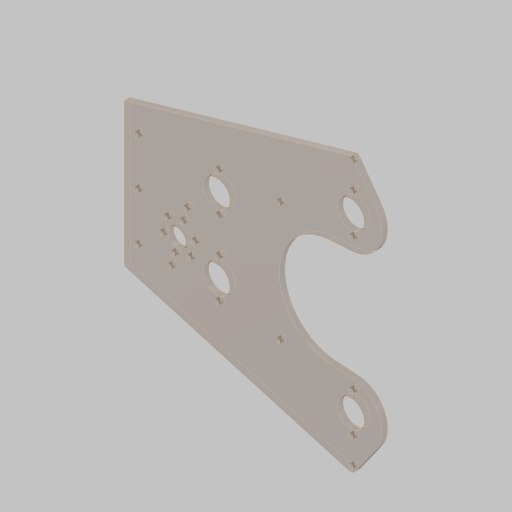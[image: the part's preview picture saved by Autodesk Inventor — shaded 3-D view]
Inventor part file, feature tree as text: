
AUTODESK INVENTOR PART (.ipt)
format: ipt  version: 2023.5 (Build 275446000, 446)  size: 201,728 bytes
history: native  units: in
note: dims shown in document units (in); Inventor stores cm internally (conversion verified against a paired STEP export)
features: sketch x1, extrude x1, hole x1
ambient origin geometry x8: Origin, YZ Plane, XZ Plane, XY Plane, X Axis, Y Axis, Z Axis, Center Point
bodies: Solid1 (feature_tree)
feature tree (3):
  sketch  "Sketch1"  dims[d0=3.0in d1=3.0in d2=4.5in d4=7.2284in d5=1.125in d6=0.75in d7=1.128in d8=1.88in d9=3.125in d10=5.6298in d11=5.992in d12=1.125in d13=0.4688in d14=0.75in d15=1.375in d16=2.3622in d18=360.0deg d20=0.25in d21=1.5in d22=1.0in d23=6.0in d24=9.5in d26=5.0in d27=0.25in d28=0.0in d29=0.375in d30=0.25in d32=1.655in d33=1.655in d34=1.655in d35=1.655in d36=1.0in d37=0.201in d38=0.75in d39=0.385in d40=0.25in d41=0.5635in d42=1.0in d43=0.8108in d44=4.0in d45=2.5in d47=0.375in d48=15.0deg d49=2.125in]
  extrude  "Extrusion1"  Depth=0.375in
  hole  "Hole1"  [1 undecoded]
note: 1 required parameter value undecoded (feature->parameter linkage not recoverable at this tier; creation-order binding heuristic only, values carry confidence <= 0.55)
